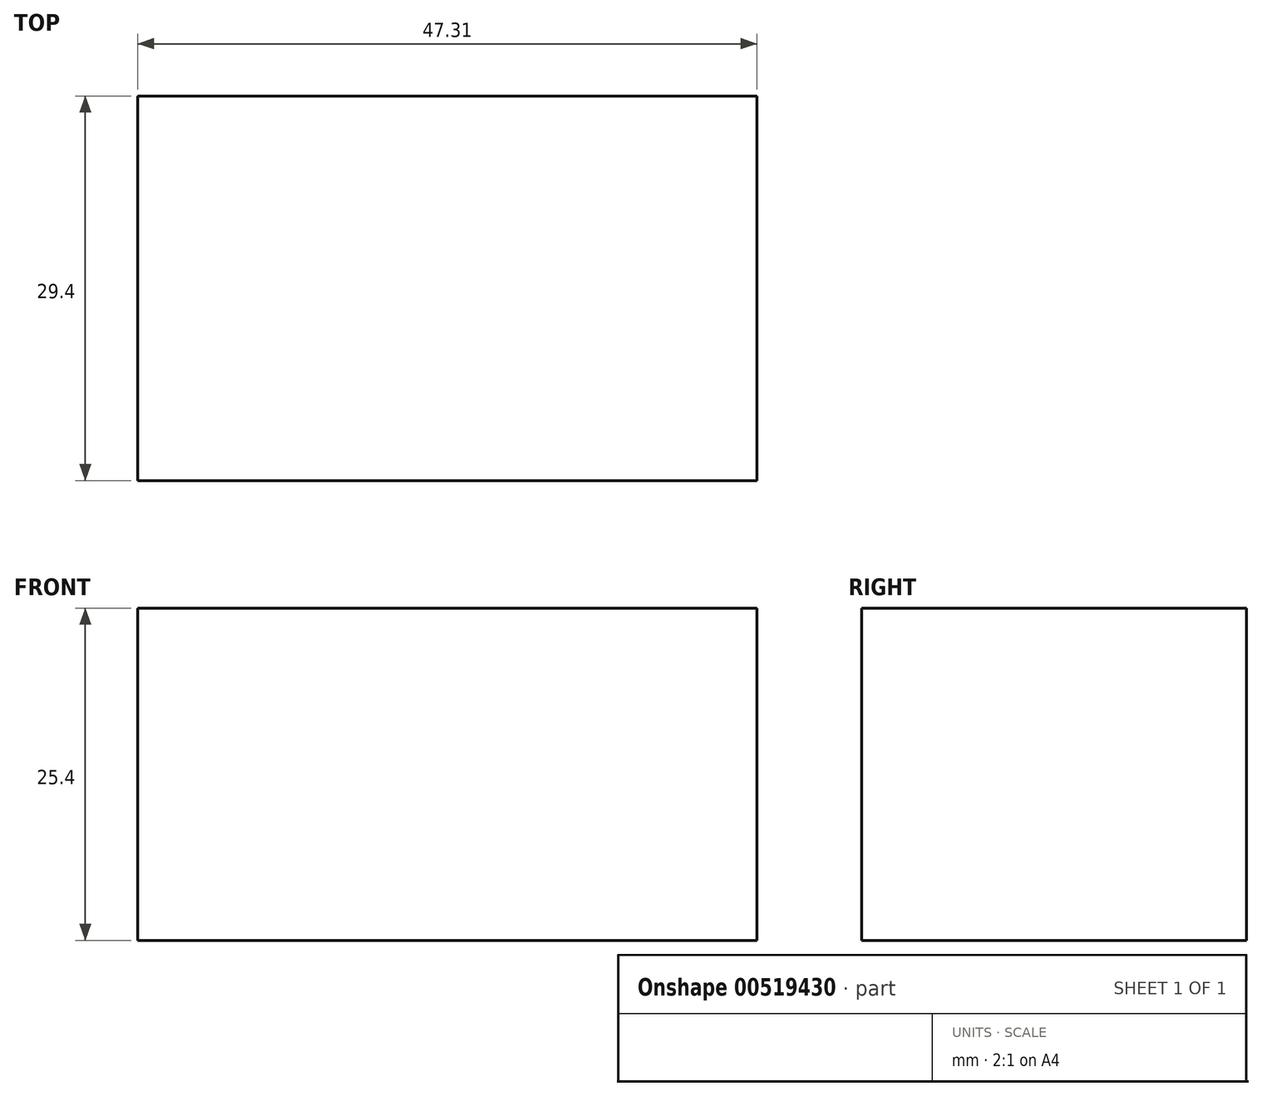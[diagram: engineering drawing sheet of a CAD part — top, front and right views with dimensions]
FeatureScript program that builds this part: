
annotation { "Feature Type Name" : "Feature", "Feature Type Description" : "" }
export const myFeature = defineFeature(function(context is Context, id is Id, definition is map)
    precondition{}
    {
        {
            var Q0;
            Q0=qCreatedBy(makeId("Top.planeOp"),FACE);
            var sketch = newSketch(context, id + "F0", { "sketchPlane" : qUnion([Q0])});
            skLineSegment(sketch, "E0.bottom", {"start": v(0, 0) * mm, "end": v(47.31, 0) * mm});
            skLineSegment(sketch, "E0.top", {"start": v(0, -29.4) * mm, "end": v(47.31, -29.4) * mm});
            skLineSegment(sketch, "E0.left", {"start": v(0, 0) * mm, "end": v(0, -29.4) * mm});
            skLineSegment(sketch, "E0.right", {"start": v(47.31, 0) * mm, "end": v(47.31, -29.4) * mm});
            skSolve(sketch);
        }
        {
            var Q0;
            Q0 = qSketchRegion(id + "F0", true);
            extrude(context, id + "F1", {"entities" : qUnion([Q0]), "depth" : 25.4 * mm, "offsetDistance" : 25.4 * mm});
        }
    });
